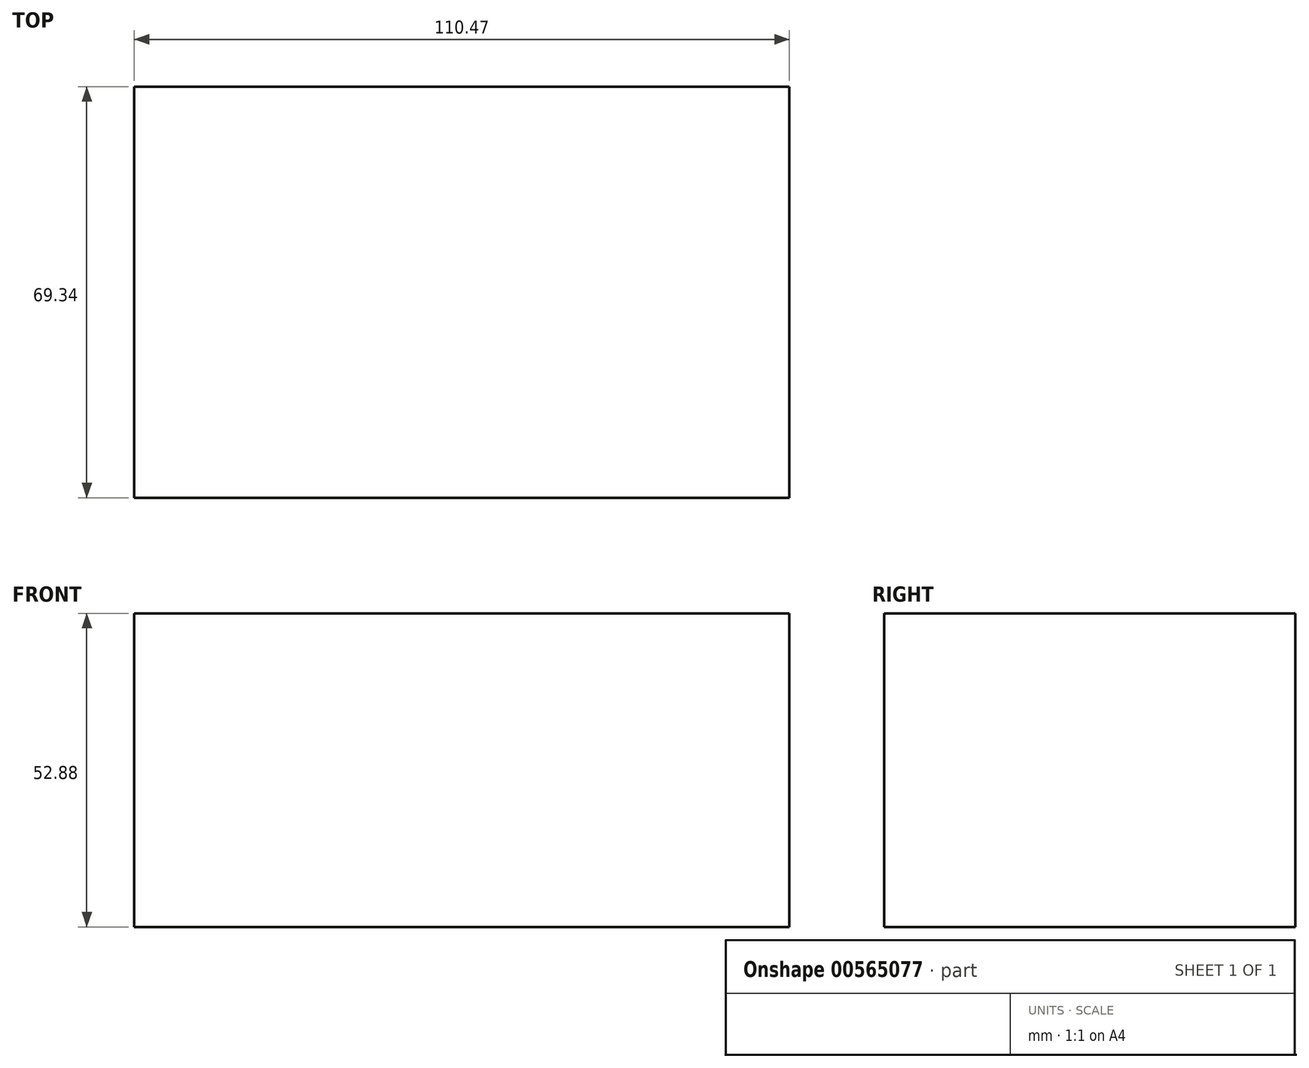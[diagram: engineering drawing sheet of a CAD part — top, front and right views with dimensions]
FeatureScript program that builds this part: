
annotation { "Feature Type Name" : "Feature", "Feature Type Description" : "" }
export const myFeature = defineFeature(function(context is Context, id is Id, definition is map)
    precondition{}
    {
        {
            var Q0;
            Q0=qCreatedBy(makeId("Front.planeOp"),FACE);
            var sketch = newSketch(context, id + "F0", { "sketchPlane" : qUnion([Q0])});
            skLineSegment(sketch, "E0.bottom", {"start": v(-110.47, -19) * mm, "end": v(0, -19) * mm});
            skLineSegment(sketch, "E0.top", {"start": v(-110.47, -71.88) * mm, "end": v(0, -71.88) * mm});
            skLineSegment(sketch, "E0.left", {"start": v(-110.47, -19) * mm, "end": v(-110.47, -71.88) * mm});
            skLineSegment(sketch, "E0.right", {"start": v(0, -19) * mm, "end": v(0, -71.88) * mm});
            skSolve(sketch);
        }
        {
            var Q0;
            Q0=makeQuery(id+"F0.imprint","IMPRINT",FACE,{"disambiguationData":[TD([[makeQuery(id+"F0.imprint","IMPRINT",EDGE,{"derivedFrom":sQuery(id+"F0.wireOp",EDGE,"E0.bottom")}),-1.0]])]});
            extrude(context, id + "F1", {"entities" : qUnion([Q0]), "depth" : 69.34 * mm, "offsetDistance" : 25.4 * mm});
        }
    });
